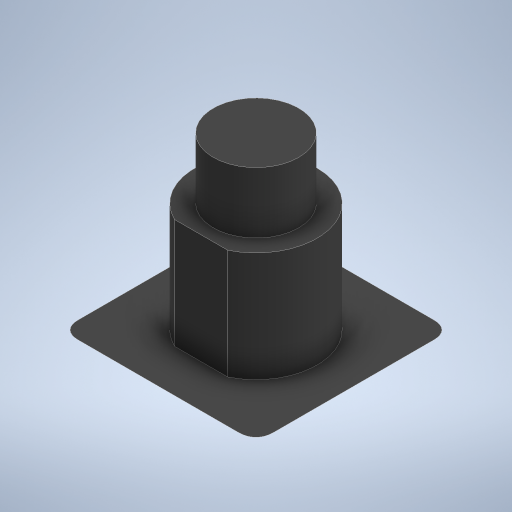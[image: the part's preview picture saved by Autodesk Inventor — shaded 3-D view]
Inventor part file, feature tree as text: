
AUTODESK INVENTOR PART (.ipt)
format: ipt  version: 2024.2 (Build 282272000, 272)  size: 289,792 bytes
history: native  units: mm
features: extrude x5, sketch x5, fillet x2, chamfer x1
ambient origin geometry x8: Origin, YZ Plane, XZ Plane, XY Plane, X Axis, Y Axis, Z Axis, Center Point
bodies: Solid1 (feature_tree)
feature tree (13):
  extrude  "Extrusion1"  Depth=9.0mm TaperAngle=0.0deg
  extrude  "Extrusion2"  Depth=5.0mm TaperAngle=0.0deg
  extrude  "Extrusion3"  Depth=16.0mm
  chamfer  "Chamfer1"  Distance=2.0mm
  fillet  "Fillet1"  Radius=2.0mm
  extrude  "Extrusion4"  Depth=2.0mm
  fillet  "Fillet2"  Radius=9.0mm
  extrude  "Extrusion5"  Depth=1.5mm TaperAngle=0.0deg
  sketch  "Sketch1"  dims[d0=10.0mm d1=9.0mm d2=0.0mm]
  sketch  "Sketch2"  dims[d3=7.0mm d4=5.0mm d5=0.0mm]
  sketch  "Sketch3"  dims[d6=16.0mm d7=16.0mm]
  sketch  "Sketch4"  dims[d8=8.0mm]
  sketch  "Sketch5"  dims[d9=8.0mm d10=2.0mm d11=0.0mm d12=2.0mm d13=2.0mm d14=45.0deg d15=2.0mm d16=9.0mm d17=1.5mm d18=0.0mm d19=0.2mm d20=4.5mm d21=9.0mm d22=0.0mm]
